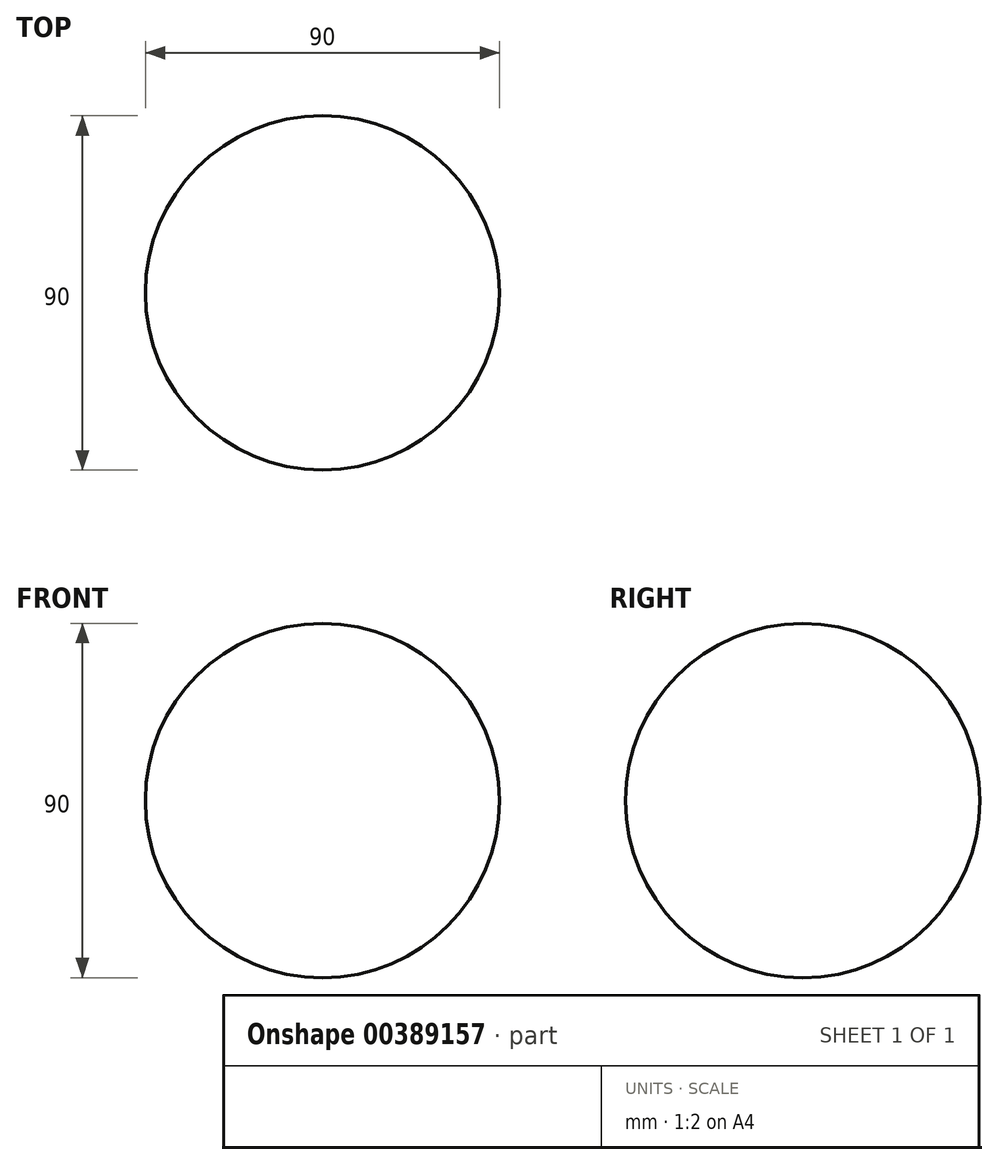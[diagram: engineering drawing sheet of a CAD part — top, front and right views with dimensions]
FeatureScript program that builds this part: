
annotation { "Feature Type Name" : "Feature", "Feature Type Description" : "" }
export const myFeature = defineFeature(function(context is Context, id is Id, definition is map)
    precondition{}
    {
        {
            var Q0;
            Q0=qCreatedBy(makeId("Front.planeOp"),FACE);
            var sketch = newSketch(context, id + "F0", { "sketchPlane" : qUnion([Q0])});
            skArc(sketch, "E0", {"start": v(0, 45) * mm, "mid": v(-45, 0) * mm, "end": v(0, -45) * mm});
            skLineSegment(sketch, "E1", {"start": v(0, 45) * mm, "end": v(0, -45) * mm});
            skSolve(sketch);
        }
        {
            var Q0;
            Q0=makeQuery(id+"F0.imprint","IMPRINT",FACE,{"disambiguationData":[TD([[makeQuery(id+"F0.imprint","IMPRINT",EDGE,{"derivedFrom":sQuery(id+"F0.wireOp",EDGE,"E0")}),1.0]])]});
            var Q1;
            Q1=sQuery(id+"F0.wireOp",EDGE,"E1");
            revolve(context, id + "F1", {"entities" : qUnion([Q0]), "axis" : qUnion([Q1]), "revolveType" : RevolveType.FULL});
        }
    });
